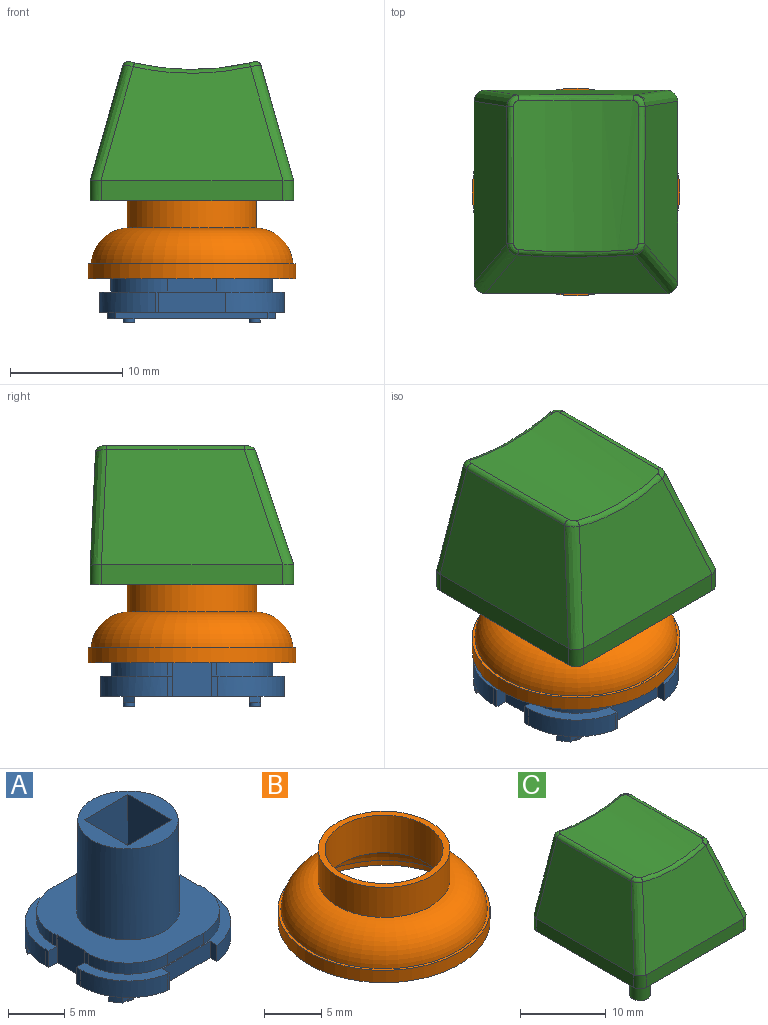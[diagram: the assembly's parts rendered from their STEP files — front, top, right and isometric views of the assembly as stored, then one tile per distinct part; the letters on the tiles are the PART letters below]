
ASSEMBLY  parts=3 mates=2
PART A: 86 faces, bbox 16.4x16.4x13.7 mm
  f0: plane 6x1.8mm, normal (0,1,0), area 10.8mm2, adj f3,f10,f11,f12
  f1: plane 1x1mm, normal (0,0,-1), area 0.8mm2, adj f13
  f2: plane 1x1mm, normal (0,0,-1), area 0.8mm2, adj f14
  f3: plane 1.8x0.85mm, normal (1,0,0), area 1.5mm2, adj f0,f11,f12,f26
  f4: plane 1.2x0.45mm, normal (-1,0,0), area 0.5mm2, adj f5,f11,f27,f28
  f5: revolved ~5x5mm, area 9.4mm2, adj f4,f6,f11,f28
  f6: plane 4.4x1.2mm, normal (0,1,0), area 5.3mm2, adj f5,f7,f11,f28
  f7: revolved ~5x5mm, area 9.4mm2, adj f6,f9,f11,f28
  f8: revolved ~9.8x9.13mm, area 277.6mm2, adj f19,f28
  f9: plane 1.2x0.45mm, normal (1,0,0), area 0.5mm2, adj f7,f11,f28,f29
  f10: plane 1.8x0.85mm, normal (-1,0,0), area 1.5mm2, adj f0,f11,f12,f31
  f11: plane 16.4x6.4mm, normal (0,0,1), area 17.2mm2, adj f0,f3,f4,f5,f6,f7,f9,f10
  f12: plane 13.52x2.05mm, normal (0,0,-1), area 17.2mm2, adj f0,f3,f10,f15,f26,f31
  f13: revolved ~1x1mm, area 0.9mm2, adj f1,f32,f33
  f14: revolved ~1x1mm, area 0.9mm2, adj f2,f33,f34
  f15: plane 13.52x0.6mm, normal (0,1,0), area 8.1mm2, adj f12,f32,f33,f34,f35,f36
  f16: plane 2.8x0.75mm, normal (0,0,-1), area 2.1mm2, adj f40,f41,f42,f43
  f17: plane 2.8x0.75mm, normal (0,0,-1), area 2.1mm2, adj f44,f45,f46,f47
  f18: plane 2.8x0.75mm, normal (0,0,-1), area 2.1mm2, adj f48,f49,f50,f51
  f19: plane 8.9x8.9mm, normal (0,0,1), area 32mm2, adj f8,f43,f47,f51,f52
  f20: plane 2.8x0.75mm, normal (0,0,-1), area 2.1mm2, adj f37,f38,f39,f52
  f21: revolved ~5x5mm, area 9.4mm2, adj f22,f24,f28,f55
  f22: plane 4.4x1.2mm, normal (0,-1,0), area 5.3mm2, adj f21,f23,f28,f55
  f23: revolved ~5x5mm, area 9.4mm2, adj f22,f28,f53,f55
  f24: plane 1.2x0.45mm, normal (1,0,0), area 0.5mm2, adj f21,f28,f55,f57
  f25: plane 1.8x0.45mm, normal (-1,0,0), area 0.8mm2, adj f11,f26,f27,f58
  f26: revolved ~5.95x5.2mm, area 15.5mm2, adj f3,f11,f12,f25,f35,f58
  f27: plane 3x1.1mm, normal (0,-1,0), area 2.1mm2, adj f4,f11,f25,f28,f58,f59,f72
  f28: plane 14.4x14.4mm, normal (0,0,1), area 119.7mm2, adj f4,f5,f6,f7,f8,f9,f21,f22
  f29: plane 3x1.1mm, normal (0,-1,0), area 2.1mm2, adj f9,f11,f28,f30,f60,f61,f72
  f30: plane 1.8x0.45mm, normal (1,0,0), area 0.8mm2, adj f11,f29,f31,f61
  f31: revolved ~5.95x5.2mm, area 15.5mm2, adj f10,f11,f12,f30,f36,f61
  f32: plane 1.86x1mm, normal (0,0,-1), area 1.1mm2, adj f13,f15,f36,f62
  f33: plane 11.2x1mm, normal (0,0,-1), area 10.4mm2, adj f13,f14,f15,f62
  f34: plane 1.85x1mm, normal (0,0,-1), area 1.1mm2, adj f14,f15,f35,f62
  f35: revolved ~1x0.69mm, area 0.7mm2, adj f15,f26,f34,f62
  f36: revolved ~1x0.69mm, area 0.7mm2, adj f15,f31,f32,f62
  f37: plane 5.9x0.75mm, normal (0,1,0), area 4.4mm2, adj f20,f38,f52,f63
  f38: plane 5.9x2.8mm, normal (1,0,0), area 16.5mm2, adj f20,f37,f39,f63
  f39: plane 5.9x0.75mm, normal (0,-1,0), area 4.4mm2, adj f20,f38,f52,f63
  f40: plane 5.9x0.75mm, normal (1,0,0), area 4.4mm2, adj f16,f41,f43,f63
  f41: plane 5.9x2.8mm, normal (0,-1,0), area 16.5mm2, adj f16,f40,f42,f63
  f42: plane 5.9x0.75mm, normal (-1,0,0), area 4.4mm2, adj f16,f41,f43,f63
  f43: plane 12.8x5.5mm, normal (0,-1,0), area 53.9mm2, adj f16,f19,f40,f42,f47,f52,f63
  f44: plane 5.9x0.75mm, normal (0,-1,0), area 4.4mm2, adj f17,f45,f47,f63
  f45: plane 5.9x2.8mm, normal (-1,0,0), area 16.5mm2, adj f17,f44,f46,f63
  f46: plane 5.9x0.75mm, normal (0,1,0), area 4.4mm2, adj f17,f45,f47,f63
  f47: plane 12.8x5.5mm, normal (-1,0,0), area 53.9mm2, adj f17,f19,f43,f44,f46,f51,f63
  f48: plane 5.9x0.75mm, normal (-1,0,0), area 4.4mm2, adj f18,f49,f51,f63
  f49: plane 5.9x2.8mm, normal (0,1,0), area 16.5mm2, adj f18,f48,f50,f63
  f50: plane 5.9x0.75mm, normal (1,0,0), area 4.4mm2, adj f18,f49,f51,f63
  f51: plane 12.8x5.5mm, normal (0,1,0), area 53.9mm2, adj f18,f19,f47,f48,f50,f52,f63
  f52: plane 12.8x5.5mm, normal (1,0,0), area 53.9mm2, adj f19,f20,f37,f39,f43,f51,f63
  f53: plane 1.2x0.45mm, normal (-1,0,0), area 0.5mm2, adj f23,f28,f55,f64
  f54: plane 1.8x0.2mm, normal (0,-1,0), area 0.4mm2, adj f55,f66,f70,f77
  f55: plane 16.4x6.45mm, normal (0,0,1), area 17.6mm2, adj f21,f22,f23,f24,f53,f54,f56,f57
  f56: plane 1.8x0.45mm, normal (1,0,0), area 0.8mm2, adj f55,f57,f69,f71
  f57: plane 3x1.1mm, normal (0,1,0), area 2.1mm2, adj f24,f28,f55,f56,f60,f71,f72
  f58: plane 3.35x1.93mm, normal (0,0,-1), area 3.5mm2, adj f25,f26,f27,f62,f72
  f59: plane 3.5x3mm, normal (-1,0,0), area 10.5mm2, adj f27,f28,f64,f72
  f60: plane 3.5x3mm, normal (1,0,0), area 10.5mm2, adj f28,f29,f57,f72
  f61: plane 3.35x1.93mm, normal (0,0,-1), area 3.5mm2, adj f29,f30,f31,f62,f72
  f62: plane 14.91x0.6mm, normal (0,-1,0), area 8.9mm2, adj f32,f33,f34,f35,f36,f58,f61,f72
  f63: plane 9.2x9.2mm, normal (0,0,-1), area 27.8mm2, adj f37,f38,f39,f40,f41,f42,f43,f44
  f64: plane 3x1.1mm, normal (0,1,0), area 2.1mm2, adj f28,f53,f55,f59,f65,f72,f73
  f65: plane 1.8x0.53mm, normal (-1,0,0), area 1mm2, adj f55,f64,f70,f73
  f66: plane 1.8x0.9mm, normal (1,0,0), area 1.6mm2, adj f54,f55,f67,f77
  f67: plane 6x1.8mm, normal (0,-1,0), area 10.8mm2, adj f55,f66,f68,f77
  f68: plane 1.8x0.85mm, normal (-1,0,0), area 1.5mm2, adj f55,f67,f69,f77
  f69: revolved ~5.95x5.2mm, area 15.5mm2, adj f55,f56,f68,f71,f75,f77
  f70: revolved ~5.92x5mm, area 15.2mm2, adj f54,f55,f65,f73,f77,f78
  f71: plane 3.35x1.93mm, normal (0,0,-1), area 3.5mm2, adj f56,f57,f69,f72,f79
  f72: plane 14.4x10.2mm, normal (0,0,-1), area 76.3mm2, adj f27,f29,f57,f58,f59,f60,f61,f62
  f73: plane 3.35x1.93mm, normal (0,0,-1), area 3.6mm2, adj f64,f65,f70,f72,f79
  f74: plane 1x1mm, normal (0,0,-1), area 0.8mm2, adj f80
  f75: revolved ~1x0.69mm, area 0.7mm2, adj f69,f76,f79,f81
  f76: plane 1.86x1mm, normal (0,0,-1), area 1.1mm2, adj f75,f79,f80,f81
  f77: plane 13.59x2.1mm, normal (0,0,-1), area 17.5mm2, adj f54,f66,f67,f68,f69,f70,f81
  f78: revolved ~1x0.67mm, area 0.7mm2, adj f70,f79,f81,f82
  f79: plane 14.95x0.6mm, normal (0,1,0), area 9mm2, adj f71,f72,f73,f75,f76,f78,f82,f83
  f80: revolved ~1x1mm, area 0.9mm2, adj f74,f76,f83
  f81: plane 13.59x0.6mm, normal (0,-1,0), area 8.2mm2, adj f75,f76,f77,f78,f82,f83
  f82: plane 1.9x1mm, normal (0,0,-1), area 1.2mm2, adj f78,f79,f81,f84
  f83: plane 11.2x1mm, normal (0,0,-1), area 10.4mm2, adj f79,f80,f81,f84
  f84: revolved ~1x1mm, area 0.9mm2, adj f82,f83,f85
  f85: plane 1x1mm, normal (0,0,-1), area 0.8mm2, adj f84
PART B: 9 faces, bbox 19.5x19.5x7.7 mm
  f0: cylinder r=9.25mm len=18.5mm, axis (0,0,1), area 76.2mm2, adj f1,f8
  f1: plane 18.5x18.5mm, normal (0,0,-1), area 41.8mm2, adj f0,f2
  f2: cylinder r=8.5mm len=17mm, axis (0,0,1), area 27.5mm2, adj f1,f3
  f3: torus R=5.16mm, axis (0,0,1), area 232.3mm2, adj f2,f4
  f4: cylinder r=5.15mm len=10.3mm, axis (0,0,1), area 129.4mm2, adj f3,f5
  f5: plane 11.5x11.5mm, normal (0,0,1), area 20.5mm2, adj f4,f6
  f6: cylinder r=5.75mm len=11.5mm, axis (0,0,1), area 115.6mm2, adj f5,f7
  f7: torus R=5.6mm, axis (0,0,1), area 243.6mm2, adj f6,f8
  f8: plane 18.5x18.5mm, normal (0,0,1), area 14.3mm2, adj f0,f7
PART C: 42 faces, bbox 22.3x23.8x26.3 mm
  f0: plane 18.1x18.1mm, normal (0,0,-1), area 67.5mm2, adj f1,f2,f3,f4,f10,f12,f14,f16
  f1: plane 16.1x1.8mm, normal (1,0,0), area 29mm2, adj f0,f8,f10,f16
  f2: plane 16.1x1.8mm, normal (0,1,0), area 29mm2, adj f0,f5,f14,f15,f16,f17
  f3: plane 16.1x1.8mm, normal (-1,0,0), area 29mm2, adj f0,f6,f12,f14
  f4: plane 16.1x1.8mm, normal (0,-1,0), area 29mm2, adj f0,f7,f10,f12
  f5: plane 16.05x10.01mm, normal (0,1,0.05), area 128.4mm2, adj f2,f15,f17,f20
  f6: bspline ~18.1x10.8mm, area 150.9mm2, adj f3,f12,f13,f14,f15,f19
  f7: plane 16.2x10.15mm, normal (0,-0.95,0.32), area 138.2mm2, adj f4,f10,f11,f12,f13,f23
  f8: bspline ~18.1x10.8mm, area 150.9mm2, adj f1,f10,f11,f16,f17,f24
  f9: cylinder r=22.9mm len=13.25mm, axis (0,-1,0), area 147.9mm2, adj f18,f19,f20,f21,f22,f23,f24,f25
  f10: cylinder r=1mm len=1.86mm, axis (0,0,-1), area 2.9mm2, adj f0,f1,f4,f7,f8,f11
  f11: bspline ~15.43x6.05mm, area 16.5mm2, adj f7,f8,f10,f25
  f12: cylinder r=1mm len=1.86mm, axis (0,0,1), area 2.9mm2, adj f0,f3,f4,f6,f7,f13
  f13: bspline ~15.43x6.05mm, area 16.5mm2, adj f6,f7,f12,f21
  f14: cylinder r=1mm len=1.81mm, axis (0,0,-1), area 2.8mm2, adj f0,f2,f3,f6,f15
  f15: bspline ~14.79x5.07mm, area 16.5mm2, adj f2,f5,f6,f14,f18
  f16: cylinder r=1mm len=1.81mm, axis (0,0,1), area 2.8mm2, adj f0,f1,f2,f8,f17
  f17: bspline ~14.79x5.07mm, area 16.5mm2, adj f2,f5,f8,f16,f22
  f18: bspline ~1.22x1.12mm, area 1mm2, adj f9,f15,f19,f20
  f19: bspline ~20.03x0.64mm, area 9.4mm2, adj f6,f9,f18,f21
  f20: bspline ~10.39x1.05mm, area 7.9mm2, adj f5,f9,f18,f22
  f21: bspline ~1.2x1.05mm, area 0.8mm2, adj f9,f13,f19,f23
  f22: bspline ~1.28x1.06mm, area 1mm2, adj f9,f17,f20,f24
  f23: bspline ~10.42x0.92mm, area 6.5mm2, adj f7,f9,f21,f25
  f24: bspline ~20.03x0.64mm, area 9.4mm2, adj f8,f9,f22,f25
  f25: bspline ~1.23x1.07mm, area 0.8mm2, adj f9,f11,f23,f24
  f26: plane 16.1x1.66mm, normal (-1,0,0), area 26.7mm2, adj f0,f27,f29,f32,f33
  f27: plane 16.1x1.78mm, normal (0,-1,0), area 28.6mm2, adj f0,f26,f28,f30,f31,f33
  f28: plane 16.1x1.66mm, normal (1,0,0), area 26.7mm2, adj f0,f27,f29,f31,f32
  f29: plane 16.1x1.64mm, normal (0,1,0), area 26.3mm2, adj f0,f26,f28,f32
  f30: plane 16.09x9.58mm, normal (0,-1,-0.05), area 122.9mm2, adj f27,f31,f33,f34
  f31: offset ~20.1x12.8mm, area 142.6mm2, adj f27,f28,f30,f32,f34
  f32: plane 16.5x10.06mm, normal (0,0.95,-0.32), area 131.7mm2, adj f26,f28,f29,f31,f33,f34
  f33: offset ~20.1x12.8mm, area 142.6mm2, adj f26,f27,f30,f32,f34
  f34: cylinder r=23.9mm len=12.41mm, axis (0,-1,0), area 104.9mm2, adj f30,f31,f32,f33,f36,f37,f38,f39
  f35: plane 5.3x5.3mm, normal (0,0,-1), area 23.6mm2, adj f36,f37,f38,f39,f40
  f36: plane 16.95x5.3mm, normal (0,1,0), area 89.3mm2, adj f34,f35,f37,f38
  f37: plane 16.95x5.3mm, normal (1,0,0), area 89.8mm2, adj f34,f35,f36,f39
  f38: plane 16.95x5.3mm, normal (-1,0,0), area 89.8mm2, adj f34,f35,f36,f39
  f39: plane 16.95x5.3mm, normal (0,-1,0), area 89.3mm2, adj f34,f35,f37,f38
  f40: cylinder r=1.2mm len=3.5mm, axis (0,0,1), area 26.4mm2, adj f35,f41
  f41: plane 2.4x2.4mm, normal (0,0,-1), area 4.5mm2, adj f40
PLACE A at identity fixed
PLACE B t=(0,0,3)mm
PLACE C t=(0,0,9.9)mm
MATE fastened A.f19 <-> C.f40  axis (0,0,1) through (0,0,12.8)mm
MATE fastened A.f28 <-> B.f0  axis (0,0,1) through (0,0,3)mm
